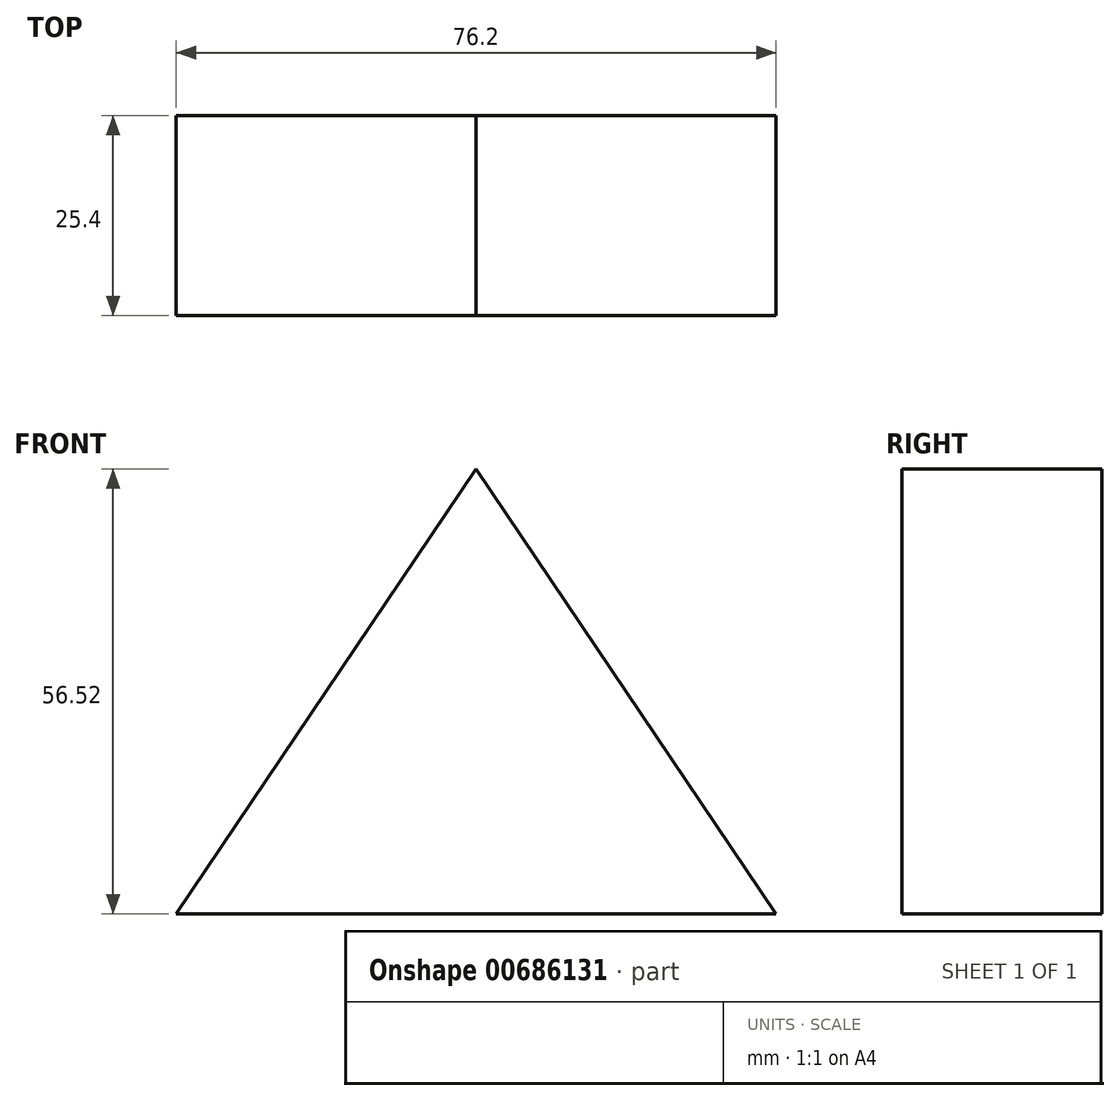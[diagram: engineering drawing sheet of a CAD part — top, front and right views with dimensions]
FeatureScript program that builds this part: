
annotation { "Feature Type Name" : "Feature", "Feature Type Description" : "" }
export const myFeature = defineFeature(function(context is Context, id is Id, definition is map)
    precondition{}
    {
        {
            var Q0;
            Q0=qCreatedBy(makeId("Front.planeOp"),FACE);
            var sketch = newSketch(context, id + "F0", { "sketchPlane" : qUnion([Q0])});
            skLineSegment(sketch, "E0", {"start": v(-38.1, 0) * mm, "end": v(0, 56.52) * mm});
            skLineSegment(sketch, "E1", {"start": v(0, 56.52) * mm, "end": v(38.1, 0) * mm});
            skLineSegment(sketch, "E2", {"start": v(-38.1, 0) * mm, "end": v(38.1, 0) * mm});
            skLineSegment(sketch, "E3", {"start": v(0, 56.52) * mm, "end": v(0, 1.96) * mm});
            skSolve(sketch);
        }
        {
            var Q0;
            Q0=makeQuery(id+"F0.imprint","IMPRINT",FACE,{"disambiguationData":[TD([[makeQuery(id+"F0.imprint","IMPRINT",EDGE,{"derivedFrom":sQuery(id+"F0.wireOp",EDGE,"E0")}),-1.0]])]});
            extrude(context, id + "F1", {"entities" : qUnion([Q0]), "depth" : 25.4 * mm, "offsetDistance" : 25.4 * mm});
        }
    });
